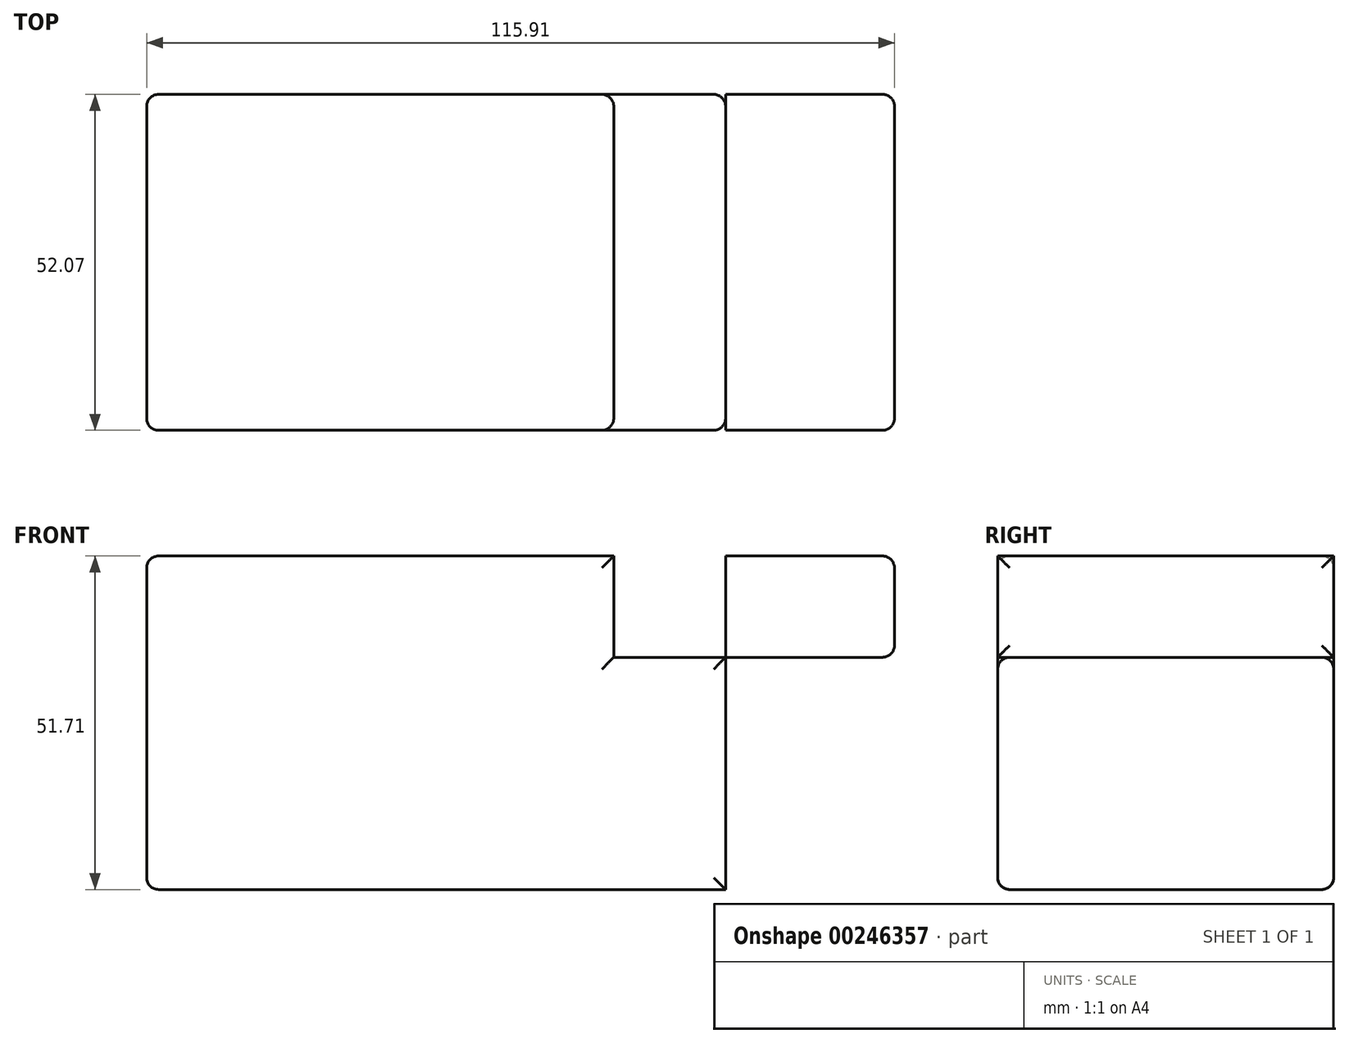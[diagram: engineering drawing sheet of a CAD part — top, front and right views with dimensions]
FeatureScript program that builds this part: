
annotation { "Feature Type Name" : "Feature", "Feature Type Description" : "" }
export const myFeature = defineFeature(function(context is Context, id is Id, definition is map)
    precondition{}
    {
        {
            var Q0;
            Q0=qCreatedBy(makeId("Front.planeOp"),FACE);
            var sketch = newSketch(context, id + "F0", { "sketchPlane" : qUnion([Q0])});
            skLineSegment(sketch, "E0.bottom", {"start": v(-75.6, 0) * mm, "end": v(-28.83, 0) * mm});
            skLineSegment(sketch, "E0.top", {"start": v(-75.6, 51.71) * mm, "end": v(-28.83, 51.71) * mm});
            skLineSegment(sketch, "E0.left", {"start": v(-75.6, 0) * mm, "end": v(-75.6, 51.71) * mm});
            skLineSegment(sketch, "E0.right", {"start": v(-28.83, 0) * mm, "end": v(-28.83, 51.71) * mm});
            skLineSegment(sketch, "E1.bottom", {"start": v(-28.83, 36) * mm, "end": v(14.14, 36) * mm});
            skLineSegment(sketch, "E1.top", {"start": v(-28.83, 0) * mm, "end": v(14.14, 0) * mm});
            skLineSegment(sketch, "E1.left", {"start": v(-28.83, 36) * mm, "end": v(-28.83, 0) * mm});
            skLineSegment(sketch, "E1.right", {"start": v(14.14, 36) * mm, "end": v(14.14, 0) * mm});
            skLineSegment(sketch, "E2.bottom", {"start": v(-28.83, 51.71) * mm, "end": v(-3.2, 51.71) * mm});
            skLineSegment(sketch, "E2.top", {"start": v(-28.83, 36) * mm, "end": v(-3.2, 36) * mm});
            skLineSegment(sketch, "E2.left", {"start": v(-28.83, 51.71) * mm, "end": v(-28.83, 36) * mm});
            skLineSegment(sketch, "E2.right", {"start": v(-3.2, 51.71) * mm, "end": v(-3.2, 36) * mm});
            skLineSegment(sketch, "E3.bottom", {"start": v(-3.2, 51.71) * mm, "end": v(14.14, 51.71) * mm});
            skLineSegment(sketch, "E3.top", {"start": v(-3.2, 36) * mm, "end": v(14.14, 36) * mm});
            skLineSegment(sketch, "E3.right", {"start": v(14.14, 51.71) * mm, "end": v(14.14, 36) * mm});
            skLineSegment(sketch, "E4.bottom", {"start": v(14.14, 51.71) * mm, "end": v(40.32, 51.71) * mm});
            skLineSegment(sketch, "E4.top", {"start": v(14.14, 36) * mm, "end": v(40.32, 36) * mm});
            skLineSegment(sketch, "E4.right", {"start": v(40.32, 51.71) * mm, "end": v(40.32, 36) * mm});
            skLineSegment(sketch, "E5.bottom", {"start": v(40.32, 36) * mm, "end": v(14.14, 36) * mm});
            skLineSegment(sketch, "E5.top", {"start": v(40.32, 0) * mm, "end": v(14.14, 0) * mm});
            skLineSegment(sketch, "E5.left", {"start": v(40.32, 36) * mm, "end": v(40.32, 0) * mm});
            skSolve(sketch);
        }
        {
            var Q0;
            Q0=makeQuery(id+"F0.imprint","IMPRINT",FACE,{"disambiguationData":[TD([[makeQuery(id+"F0.imprint","IMPRINT",EDGE,{"derivedFrom":sQuery(id+"F0.wireOp",EDGE,"E4.bottom")}),-1.0]])]});
            var Q1;
            Q1=makeQuery(id+"F0.imprint","IMPRINT",FACE,{"disambiguationData":[TD([[makeQuery(id+"F0.imprint","IMPRINT",EDGE,{"derivedFrom":sQuery(id+"F0.wireOp",EDGE,"E5.bottom")}),1.0]])]});
            var Q2;
            Q2=makeQuery(id+"F0.imprint","IMPRINT",FACE,{"disambiguationData":[TD([[makeQuery(id+"F0.imprint","IMPRINT",EDGE,{"derivedFrom":sQuery(id+"F0.wireOp",EDGE,"E1.top")}),1.0]])]});
            var Q3;
            Q3=makeQuery(id+"F0.imprint","IMPRINT",FACE,{"disambiguationData":[TD([[makeQuery(id+"F0.imprint","IMPRINT",EDGE,{"derivedFrom":sQuery(id+"F0.wireOp",EDGE,"E2.bottom")}),-1.0]])]});
            var Q4;
            Q4=makeQuery(id+"F0.imprint","IMPRINT",FACE,{"disambiguationData":[TD([[makeQuery(id+"F0.imprint","IMPRINT",EDGE,{"derivedFrom":sQuery(id+"F0.wireOp",EDGE,"E0.bottom")}),1.0]])]});
            extrude(context, id + "F1", {"entities" : qUnion([Q0, Q1, Q2, Q3, Q4]), "depth" : 52.07 * mm});
        }
        {
            var Q0;
            Q0=makeQuery(id+"F1.opExtrude","CAP_FACE",FACE,{"disambiguationData":[OSD([sQuery(id+"F0.wireOp",EDGE,"E0.bottom"),sQuery(id+"F0.wireOp",EDGE,"E0.top"),sQuery(id+"F0.wireOp",EDGE,"E0.left"),sQuery(id+"F0.wireOp",EDGE,"E1.top"),sQuery(id+"F0.wireOp",EDGE,"E2.bottom"),sQuery(id+"F0.wireOp",EDGE,"E3.top"),sQuery(id+"F0.wireOp",EDGE,"E2.right"),sQuery(id+"F0.wireOp",EDGE,"E4.bottom"),sQuery(id+"F0.wireOp",EDGE,"E3.right"),sQuery(id+"F0.wireOp",EDGE,"E4.right"),sQuery(id+"F0.wireOp",EDGE,"E5.top"),sQuery(id+"F0.wireOp",EDGE,"E5.left")])],"isStart":true});
            var Q1;
            Q1=makeQuery(id+"F1.opExtrude","CAP_FACE",FACE,{"disambiguationData":[OSD([sQuery(id+"F0.wireOp",EDGE,"E0.bottom"),sQuery(id+"F0.wireOp",EDGE,"E0.top"),sQuery(id+"F0.wireOp",EDGE,"E0.left"),sQuery(id+"F0.wireOp",EDGE,"E1.top"),sQuery(id+"F0.wireOp",EDGE,"E2.bottom"),sQuery(id+"F0.wireOp",EDGE,"E3.top"),sQuery(id+"F0.wireOp",EDGE,"E2.right"),sQuery(id+"F0.wireOp",EDGE,"E4.bottom"),sQuery(id+"F0.wireOp",EDGE,"E3.right"),sQuery(id+"F0.wireOp",EDGE,"E4.right"),sQuery(id+"F0.wireOp",EDGE,"E5.top"),sQuery(id+"F0.wireOp",EDGE,"E5.left")])],"isStart":false});
            var Q2;
            Q2=makeQuery(id+"F1.opExtrude","SWEPT_FACE",FACE,{"disambiguationData":[OSD([sQuery(id+"F0.wireOp",EDGE,"E4.right"),sQuery(id+"F0.wireOp",EDGE,"E5.left")])]});
            var Q3;
            Q3=makeQuery(id+"F1.opExtrude","SWEPT_FACE",FACE,{"disambiguationData":[OSD([sQuery(id+"F0.wireOp",EDGE,"E0.left")])]});
            fillet(context, id + "F2", {"entities" : qUnion([Q0, Q1, Q2, Q3]), "radius" : 1.84 * mm, "tangentPropagation" : true, "allowEdgeOverflow" : false});
        }
    });
